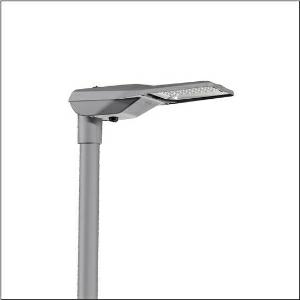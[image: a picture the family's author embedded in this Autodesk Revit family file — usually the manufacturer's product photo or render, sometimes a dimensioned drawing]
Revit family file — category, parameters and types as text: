
# Revit family: streetlight_sl_21_mini___st0_8a_5xe2c33t08jb_bac6
name_source: partatom
category: Lighting Fixtures
units: mm (PartAtom-declared; Revit-internal decimal feet)

## family parameters
Cut with Voids When Loaded = No
Host = Face
Light Source = No
Part Type = Normal
Room Calculation Point = No
Round Connector Dimension = Use Diameter
Shared = No

## types (1)
- --- (1 x LED, 12940 lm, 88.6 W, 3000K)
    Apparent Load = 89 VA
    CIE Flux Codes = 41 75 97 100 100
    Color Rendering = 70
    Color Temperature = 3000K
    Default Elevation = 1800 mm
    Description = Streetlight SL 21 mini, mast luminaire, primary light control with lens, of PMMA, primary optical cover: cover, of toughened safety glass, transparent, light distribution: ST0.8a, light emission: direct distribution, primary light characteristic: asymmetric, installation type: side-entry, post-top, LED, High Power LED, rated luminous flux: 12.940lm, luminous efficacy: 146lm/W, light colour: 730, colour temperature: 3000K, control gear: D4i, control: overheat protection, constant luminous flux control, time-dependent luminous flux control, flexible luminous flux parameterisation, pre-setting: logarithmic dimming characteristic, mains connection: 220..240V, AC, 50/60Hz, start of lifetime: 89W, end of service life: 92W, reduction: 41W, luminaire housing, of diecast aluminium, powder-coated, Siteco® metallic grey (DB 702S), corrosivity category C5 mid according to DIN EN ISO 12944, please order mast flange separately, inclination adjustable: 0°, 5°, 10°, 15°, sealing non-destructively replaceable, multi-level sealing system, length: 628mm, width: 235mm, height: 110mm, mast flange for spigot size: 42mm (side-entry): 5XC10008XM4, 60/48mm (side-entry/post-top): 5XC10108XM2, 76/60mm (side-entry/post-top): 5XC10108XM1, mounting height: 4..8m, Smart Interface below and above, protection rating (complete): IP66, insulation class (complete): insulation class II (safety insulation), certification: CE, ENEC, ENEC+, VDE, impact resistance: IK10, permissible operating ambient temperature for outdoor applications: -40..+50°C, standard-compliant lighting for roads and squares, packaging unit: 1 piece

Light Distribution: ST0.8a
    Height = 110 mm
    Lamp = 1 x LED
    Lamp Light Flux = 12940 lm
    Lamp Power = 88.6 W
    Lamp count = 1
    Length = 625 mm
    Luminous efficacy = 146 lm/W
    Manufacturer = Siteco
    ModVariant = No
    Model = 5XE2C33T08JB
    Number of Poles = 1
    OnlyDefault = Yes
    Power Factor = 1
    Product Name = Streetlight SL 21 mini | ST0.8a
    Product group = mast luminaire | pylon top
    ProductGroupID = 6100
    Protection Class = Protection class II
    Protection Degree = IP 66
    RLX_Detail_Level = 1
    RLX_Emergency_Light_Flux = 0 lm
    RLX_Emergency_Type = 0
    RLX_Emergency_Type_DB = No
    RlxData = <blob elided: 26353 chars, md5=e453932a>
    Socket = socket
    Standby Power = 0 W
    System Light Flux = 12940 lm
    System Power = 89 W
    Type Comments = factory setting: luminous flux: 100 % | dim-lin: 254 | 915 mA
    Type Image = l_1003514.jpg
    URL = http://relux.com
    VarID = @adj_030945
    Voltage = 0 V
    Weight = 0.00 kg
    Width = 234 mm

## geometry (parser evidence)
native form markers: Blend x4, Sweep x12
no freeform markers — native parametric forms only
